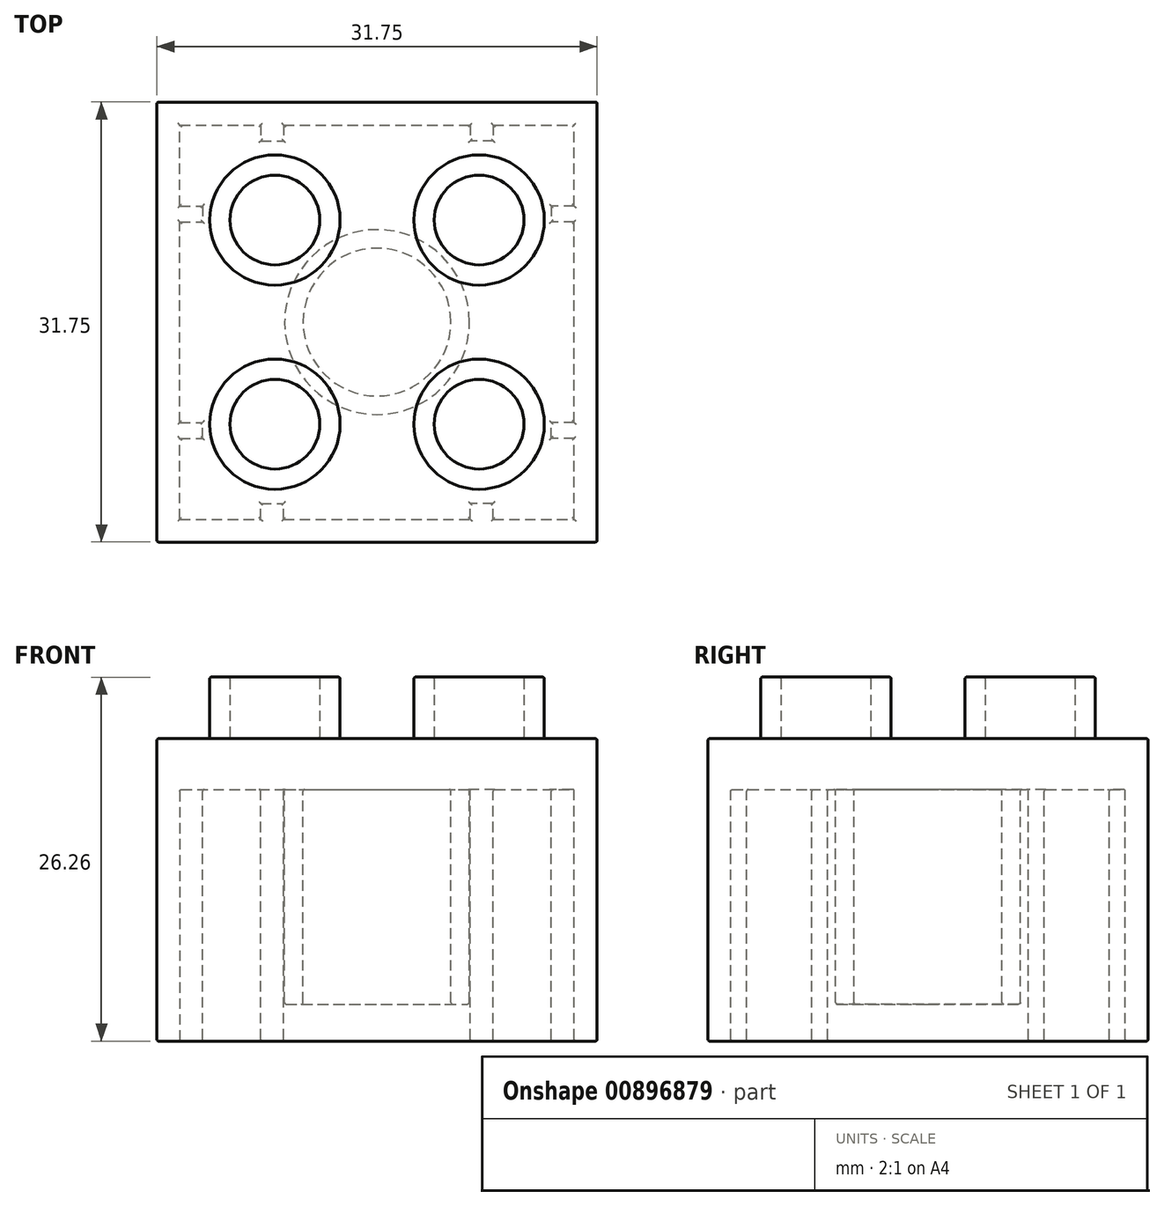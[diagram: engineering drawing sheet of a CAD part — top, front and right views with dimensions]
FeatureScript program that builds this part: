
annotation { "Feature Type Name" : "Feature", "Feature Type Description" : "" }
export const myFeature = defineFeature(function(context is Context, id is Id, definition is map)
    precondition{}
    {
        {
            var Q0;
            Q0=qCreatedBy(makeId("Top.planeOp"),FACE);
            var sketch = newSketch(context, id + "F0", { "sketchPlane" : qUnion([Q0])});
            skLineSegment(sketch, "E0.bottom", {"start": v(-34.78, 34.87) * mm, "end": v(-66.53, 34.87) * mm});
            skLineSegment(sketch, "E0.top", {"start": v(-34.78, 3.12) * mm, "end": v(-66.53, 3.12) * mm});
            skLineSegment(sketch, "E0.left", {"start": v(-34.78, 34.87) * mm, "end": v(-34.78, 3.12) * mm});
            skLineSegment(sketch, "E0.right", {"start": v(-66.53, 34.87) * mm, "end": v(-66.53, 3.12) * mm});
            skSolve(sketch);
        }
        {
            var Q0;
            Q0=makeQuery(id+"F0.imprint","IMPRINT",FACE,{"disambiguationData":[TD([[makeQuery(id+"F0.imprint","IMPRINT",EDGE,{"derivedFrom":sQuery(id+"F0.wireOp",EDGE,"E0.bottom")}),1.0]])]});
            extrude(context, id + "F1", {"entities" : qUnion([Q0]), "depth" : 21.82 * mm, "offsetDistance" : 25.4 * mm});
        }
        {
            var Q0;
            Q0=makeQuery(id+"F1.opExtrude","CAP_FACE",FACE,{"disambiguationData":[OSD([sQuery(id+"F0.wireOp",EDGE,"E0.bottom"),sQuery(id+"F0.wireOp",EDGE,"E0.top"),sQuery(id+"F0.wireOp",EDGE,"E0.left"),sQuery(id+"F0.wireOp",EDGE,"E0.right")])],"isStart":false});
            var sketch = newSketch(context, id + "F2", { "sketchPlane" : qUnion([Q0])});
            skCircle(sketch, "E1", {"center": v(-58.02, 26.36) * mm, "radius": 4.7 * mm});
            skCircle(sketch, "E2", {"center": v(-58.02, 26.36) * mm, "radius": 3.24 * mm});
            skCircle(sketch, "E3", {"center": v(-43.29, 26.36) * mm, "radius": 4.7 * mm});
            skCircle(sketch, "E4", {"center": v(-43.29, 26.36) * mm, "radius": 3.24 * mm});
            skCircle(sketch, "E5", {"center": v(-58.02, 11.63) * mm, "radius": 4.7 * mm});
            skCircle(sketch, "E6", {"center": v(-58.02, 11.63) * mm, "radius": 3.24 * mm});
            skCircle(sketch, "E7", {"center": v(-43.29, 11.63) * mm, "radius": 4.7 * mm});
            skCircle(sketch, "E8", {"center": v(-43.29, 11.63) * mm, "radius": 3.24 * mm});
            skSolve(sketch);
        }
        {
            var Q0;
            Q0=makeQuery(id+"F2.imprint","IMPRINT",FACE,{"disambiguationData":[TD([[makeQuery(id+"F2.imprint","IMPRINT",EDGE,{"derivedFrom":sQuery(id+"F2.wireOp",EDGE,"E7")}),1.0]])]});
            var Q1;
            Q1=makeQuery(id+"F2.imprint","IMPRINT",FACE,{"disambiguationData":[TD([[makeQuery(id+"F2.imprint","IMPRINT",EDGE,{"derivedFrom":sQuery(id+"F2.wireOp",EDGE,"E5")}),1.0]])]});
            var Q2;
            Q2=makeQuery(id+"F2.imprint","IMPRINT",FACE,{"disambiguationData":[TD([[makeQuery(id+"F2.imprint","IMPRINT",EDGE,{"derivedFrom":sQuery(id+"F2.wireOp",EDGE,"E1")}),1.0]])]});
            var Q3;
            Q3=makeQuery(id+"F2.imprint","IMPRINT",FACE,{"disambiguationData":[TD([[makeQuery(id+"F2.imprint","IMPRINT",EDGE,{"derivedFrom":sQuery(id+"F2.wireOp",EDGE,"E3")}),1.0]])]});
            extrude(context, id + "F3", {"entities" : qUnion([Q0, Q1, Q2, Q3]), "operationType" : NewBodyOperationType.ADD, "depth" : 4.44 * mm, "offsetDistance" : 25.4 * mm});
        }
        {
            var Q0;
            Q0=makeQuery(id+"F1.opExtrude","CAP_FACE",FACE,{"disambiguationData":[OSD([sQuery(id+"F0.wireOp",EDGE,"E0.bottom"),sQuery(id+"F0.wireOp",EDGE,"E0.top"),sQuery(id+"F0.wireOp",EDGE,"E0.left"),sQuery(id+"F0.wireOp",EDGE,"E0.right")])],"isStart":true});
            var sketch = newSketch(context, id + "F4", { "sketchPlane" : qUnion([Q0])});
            skLineSegment(sketch, "E9.bottom", {"start": v(-64.88, -4.77) * mm, "end": v(-36.43, -4.77) * mm});
            skLineSegment(sketch, "E9.top", {"start": v(-64.88, -33.22) * mm, "end": v(-36.43, -33.22) * mm});
            skLineSegment(sketch, "E9.left", {"start": v(-64.88, -4.77) * mm, "end": v(-64.88, -33.22) * mm});
            skLineSegment(sketch, "E9.right", {"start": v(-36.43, -4.77) * mm, "end": v(-36.43, -33.22) * mm});
            skSolve(sketch);
        }
        {
            var Q0;
            Q0=makeQuery(id+"F4.imprint","IMPRINT",FACE,{"disambiguationData":[TD([[makeQuery(id+"F4.imprint","IMPRINT",EDGE,{"derivedFrom":sQuery(id+"F4.wireOp",EDGE,"E9.bottom")}),-1.0]])]});
            extrude(context, id + "F5", {"entities" : qUnion([Q0]), "operationType" : NewBodyOperationType.REMOVE, "oppositeDirection" : true, "depth" : 18.16 * mm, "offsetDistance" : 25.4 * mm});
        }
        {
            var Q0;
            Q0=makeQuery(id+"F5.boolean.opBoolean","COPY",FACE,{"derivedFrom":makeQuery(id+"F5.opExtrude","CAP_FACE",FACE,{"disambiguationData":[OSD([sQuery(id+"F4.wireOp",EDGE,"E9.bottom"),sQuery(id+"F4.wireOp",EDGE,"E9.top"),sQuery(id+"F4.wireOp",EDGE,"E9.left"),sQuery(id+"F4.wireOp",EDGE,"E9.right")])],"isStart":false})});
            var sketch = newSketch(context, id + "F6", { "sketchPlane" : qUnion([Q0])});
            skCircle(sketch, "E10", {"center": v(-50.65, -19) * mm, "radius": 5.33 * mm});
            skCircle(sketch, "E11", {"center": v(-50.65, -19) * mm, "radius": 6.67 * mm});
            skSolve(sketch);
        }
        {
            var Q0;
            Q0=makeQuery(id+"F6.imprint","IMPRINT",FACE,{"disambiguationData":[TD([[makeQuery(id+"F6.imprint","IMPRINT",EDGE,{"derivedFrom":sQuery(id+"F6.wireOp",EDGE,"E10")}),-1.0]])]});
            extrude(context, id + "F7", {"entities" : qUnion([Q0]), "operationType" : NewBodyOperationType.ADD, "depth" : 15.5 * mm, "offsetDistance" : 25.4 * mm});
        }
        {
            var Q0;
            {var subQ0=sQuery(id+"F4.wireOp",EDGE,"E9.right");var subQ1=sQuery(id+"F4.wireOp",EDGE,"E9.left");var subQ2=sQuery(id+"F4.wireOp",EDGE,"E9.top");var subQ3=sQuery(id+"F4.wireOp",EDGE,"E9.bottom");Q0=makeQuery(id+"F7.boolean.opBoolean","SPLIT",FACE,{"disambiguationData":[TD([makeQuery(id+"F5.boolean.opBoolean","COPY",FACE,{"derivedFrom":makeQuery(id+"F5.opExtrude","SWEPT_FACE",FACE,{"disambiguationData":[OSD([subQ3])]})})])],"derivedFrom":makeQuery(id+"F5.boolean.opBoolean","COPY",FACE,{"derivedFrom":makeQuery(id+"F5.opExtrude","CAP_FACE",FACE,{"disambiguationData":[OSD([subQ3,subQ2,subQ1,subQ0])],"isStart":false})})});}
            var sketch = newSketch(context, id + "F8", { "sketchPlane" : qUnion([Q0])});
            skLineSegment(sketch, "E12.bottom", {"start": v(-36.43, -10.61) * mm, "end": v(-38.08, -10.61) * mm});
            skLineSegment(sketch, "E12.top", {"start": v(-36.43, -11.75) * mm, "end": v(-38.08, -11.75) * mm});
            skLineSegment(sketch, "E12.left", {"start": v(-36.43, -10.61) * mm, "end": v(-36.43, -11.75) * mm});
            skLineSegment(sketch, "E12.right", {"start": v(-38.08, -10.61) * mm, "end": v(-38.08, -11.75) * mm});
            skLineSegment(sketch, "E13.bottom", {"start": v(-42.27, -4.77) * mm, "end": v(-43.92, -4.77) * mm});
            skLineSegment(sketch, "E13.top", {"start": v(-42.27, -5.91) * mm, "end": v(-43.92, -5.91) * mm});
            skLineSegment(sketch, "E13.left", {"start": v(-42.27, -4.77) * mm, "end": v(-42.27, -5.91) * mm});
            skLineSegment(sketch, "E13.right", {"start": v(-43.92, -4.77) * mm, "end": v(-43.92, -5.91) * mm});
            skLineSegment(sketch, "E14", {"start": v(-50.65, -4.77) * mm, "end": v(-50.65, -33.22) * mm});
            skLineSegment(sketch, "E15", {"start": v(-64.88, -19) * mm, "end": v(-36.43, -19) * mm});
            skLineSegment(sketch, "E16.MirrorCS", {"start": v(-59.04, -4.77) * mm, "end": v(-59.04, -5.91) * mm});
            skLineSegment(sketch, "E17.MirrorCS", {"start": v(-59.04, -4.77) * mm, "end": v(-57.38, -4.77) * mm});
            skLineSegment(sketch, "E18.MirrorCS", {"start": v(-57.38, -4.77) * mm, "end": v(-57.38, -5.91) * mm});
            skLineSegment(sketch, "E19.MirrorCS", {"start": v(-59.04, -5.91) * mm, "end": v(-57.38, -5.91) * mm});
            skLineSegment(sketch, "E20.MirrorCS", {"start": v(-63.23, -10.61) * mm, "end": v(-63.23, -11.75) * mm});
            skLineSegment(sketch, "E21.MirrorCS", {"start": v(-64.88, -10.61) * mm, "end": v(-63.23, -10.61) * mm});
            skLineSegment(sketch, "E22.MirrorCS", {"start": v(-64.88, -10.61) * mm, "end": v(-64.88, -11.75) * mm});
            skLineSegment(sketch, "E23.MirrorCS", {"start": v(-64.88, -11.75) * mm, "end": v(-63.23, -11.75) * mm});
            skLineSegment(sketch, "E24.MirrorCS", {"start": v(-42.27, -33.22) * mm, "end": v(-42.27, -32.07) * mm});
            skLineSegment(sketch, "E25.MirrorCS", {"start": v(-43.92, -33.22) * mm, "end": v(-43.92, -32.07) * mm});
            skLineSegment(sketch, "E26.MirrorCS", {"start": v(-42.27, -33.22) * mm, "end": v(-43.92, -33.22) * mm});
            skLineSegment(sketch, "E27.MirrorCS", {"start": v(-42.27, -32.07) * mm, "end": v(-43.92, -32.07) * mm});
            skLineSegment(sketch, "E28.MirrorCS", {"start": v(-38.08, -27.37) * mm, "end": v(-38.08, -26.23) * mm});
            skLineSegment(sketch, "E29.MirrorCS", {"start": v(-36.43, -27.37) * mm, "end": v(-38.08, -27.37) * mm});
            skLineSegment(sketch, "E30.MirrorCS", {"start": v(-36.43, -27.37) * mm, "end": v(-36.43, -26.23) * mm});
            skLineSegment(sketch, "E31.MirrorCS", {"start": v(-36.43, -26.23) * mm, "end": v(-38.08, -26.23) * mm});
            skLineSegment(sketch, "E32.MirrorCS", {"start": v(-63.23, -27.37) * mm, "end": v(-63.23, -26.23) * mm});
            skLineSegment(sketch, "E33.MirrorCS", {"start": v(-64.88, -26.23) * mm, "end": v(-63.23, -26.23) * mm});
            skLineSegment(sketch, "E34.MirrorCS", {"start": v(-64.88, -27.37) * mm, "end": v(-64.88, -26.23) * mm});
            skLineSegment(sketch, "E35.MirrorCS", {"start": v(-64.88, -27.37) * mm, "end": v(-63.23, -27.37) * mm});
            skLineSegment(sketch, "E36.MirrorCS", {"start": v(-59.04, -33.22) * mm, "end": v(-59.04, -32.07) * mm});
            skLineSegment(sketch, "E37.MirrorCS", {"start": v(-59.04, -33.22) * mm, "end": v(-57.38, -33.22) * mm});
            skLineSegment(sketch, "E38.MirrorCS", {"start": v(-57.38, -33.22) * mm, "end": v(-57.38, -32.07) * mm});
            skLineSegment(sketch, "E39.MirrorCS", {"start": v(-59.04, -32.07) * mm, "end": v(-57.38, -32.07) * mm});
            skSolve(sketch);
        }
        {
            var Q0;
            Q0=makeQuery(id+"F8.imprint","IMPRINT",FACE,{"disambiguationData":[TD([[makeQuery(id+"F8.imprint","IMPRINT",EDGE,{"derivedFrom":sQuery(id+"F8.wireOp",EDGE,"E13.bottom")}),-1.0]])]});
            var Q1;
            Q1=makeQuery(id+"F8.imprint","IMPRINT",FACE,{"disambiguationData":[TD([[makeQuery(id+"F8.imprint","IMPRINT",EDGE,{"derivedFrom":sQuery(id+"F8.wireOp",EDGE,"E12.bottom")}),1.0]])]});
            var Q2;
            Q2=makeQuery(id+"F8.imprint","IMPRINT",FACE,{"disambiguationData":[TD([[makeQuery(id+"F8.imprint","IMPRINT",EDGE,{"derivedFrom":sQuery(id+"F8.wireOp",EDGE,"E16.MirrorCS")}),1.0]])]});
            var Q3;
            Q3=makeQuery(id+"F8.imprint","IMPRINT",FACE,{"disambiguationData":[TD([[makeQuery(id+"F8.imprint","IMPRINT",EDGE,{"derivedFrom":sQuery(id+"F8.wireOp",EDGE,"E20.MirrorCS")}),-1.0]])]});
            var Q4;
            Q4=makeQuery(id+"F8.imprint","IMPRINT",FACE,{"disambiguationData":[TD([[makeQuery(id+"F8.imprint","IMPRINT",EDGE,{"derivedFrom":sQuery(id+"F8.wireOp",EDGE,"E32.MirrorCS")}),1.0]])]});
            var Q5;
            Q5=makeQuery(id+"F8.imprint","IMPRINT",FACE,{"disambiguationData":[TD([[makeQuery(id+"F8.imprint","IMPRINT",EDGE,{"derivedFrom":sQuery(id+"F8.wireOp",EDGE,"E36.MirrorCS")}),-1.0]])]});
            var Q6;
            Q6=makeQuery(id+"F8.imprint","IMPRINT",FACE,{"disambiguationData":[TD([[makeQuery(id+"F8.imprint","IMPRINT",EDGE,{"derivedFrom":sQuery(id+"F8.wireOp",EDGE,"E24.MirrorCS")}),1.0]])]});
            var Q7;
            Q7=makeQuery(id+"F8.imprint","IMPRINT",FACE,{"disambiguationData":[TD([[makeQuery(id+"F8.imprint","IMPRINT",EDGE,{"derivedFrom":sQuery(id+"F8.wireOp",EDGE,"E28.MirrorCS")}),-1.0]])]});
            extrude(context, id + "F9", {"entities" : qUnion([Q0, Q1, Q2, Q3, Q4, Q5, Q6, Q7]), "operationType" : NewBodyOperationType.ADD, "depth" : 18.16 * mm, "offsetDistance" : 25.4 * mm});
        }
        {
            var Q0;
            Q0=makeQuery(id+"F3.opExtrude","SWEPT_FACE",FACE,{"disambiguationData":[OSD([sQuery(id+"F2.wireOp",EDGE,"E1")])]});
            var Q1;
            Q1=makeQuery(id+"F3.opExtrude","SWEPT_FACE",FACE,{"disambiguationData":[OSD([sQuery(id+"F2.wireOp",EDGE,"E2")])]});
            var Q2;
            Q2=makeQuery(id+"F3.opExtrude","SWEPT_FACE",FACE,{"disambiguationData":[OSD([sQuery(id+"F2.wireOp",EDGE,"E3")])]});
            var Q3;
            Q3=makeQuery(id+"F3.opExtrude","SWEPT_FACE",FACE,{"disambiguationData":[OSD([sQuery(id+"F2.wireOp",EDGE,"E4")])]});
            var Q4;
            Q4=makeQuery(id+"F3.opExtrude","SWEPT_FACE",FACE,{"disambiguationData":[OSD([sQuery(id+"F2.wireOp",EDGE,"E7")])]});
            var Q5;
            Q5=makeQuery(id+"F3.opExtrude","SWEPT_FACE",FACE,{"disambiguationData":[OSD([sQuery(id+"F2.wireOp",EDGE,"E8")])]});
            var Q6;
            Q6=makeQuery(id+"F3.opExtrude","SWEPT_FACE",FACE,{"disambiguationData":[OSD([sQuery(id+"F2.wireOp",EDGE,"E5")])]});
            var Q7;
            Q7=makeQuery(id+"F3.opExtrude","SWEPT_FACE",FACE,{"disambiguationData":[OSD([sQuery(id+"F2.wireOp",EDGE,"E6")])]});
            var Q8;
            {var subQ0=sQuery(id+"F0.wireOp",EDGE,"E0.left");var subQ1=sQuery(id+"F0.wireOp",EDGE,"E0.top");var subQ2=sQuery(id+"F0.wireOp",EDGE,"E0.right");var subQ3=sQuery(id+"F0.wireOp",EDGE,"E0.bottom");Q8=makeQuery(id+"F3.boolean.opBoolean","SPLIT",FACE,{"disambiguationData":[TD([makeQuery(id+"F1.opExtrude","SWEPT_FACE",FACE,{"disambiguationData":[OSD([subQ3])]})])],"derivedFrom":makeQuery(id+"F1.opExtrude","CAP_FACE",FACE,{"disambiguationData":[OSD([subQ3,subQ1,subQ0,subQ2])],"isStart":false})});}
            var Q9;
            Q9=makeQuery(id+"F1.opExtrude","SWEPT_FACE",FACE,{"disambiguationData":[OSD([sQuery(id+"F0.wireOp",EDGE,"E0.right")])]});
            var Q10;
            Q10=makeQuery(id+"F1.opExtrude","SWEPT_FACE",FACE,{"disambiguationData":[OSD([sQuery(id+"F0.wireOp",EDGE,"E0.top")])]});
            var Q11;
            Q11=makeQuery(id+"F1.opExtrude","SWEPT_FACE",FACE,{"disambiguationData":[OSD([sQuery(id+"F0.wireOp",EDGE,"E0.left")])]});
            var Q12;
            Q12=makeQuery(id+"F1.opExtrude","SWEPT_FACE",FACE,{"disambiguationData":[OSD([sQuery(id+"F0.wireOp",EDGE,"E0.bottom")])]});
            var Q13;
            Q13=makeQuery(id+"F7.opExtrude","SWEPT_FACE",FACE,{"disambiguationData":[OSD([sQuery(id+"F6.wireOp",EDGE,"E10")])]});
            var Q14;
            Q14=makeQuery(id+"F7.opExtrude","SWEPT_FACE",FACE,{"disambiguationData":[OSD([sQuery(id+"F6.wireOp",EDGE,"E11")])]});
            var Q15;
            Q15=makeQuery(id+"F9.boolean.opBoolean","MERGE",FACE,{"derivedFrom":[makeQuery(id+"F1.opExtrude","CAP_FACE",FACE,{"disambiguationData":[OSD([sQuery(id+"F0.wireOp",EDGE,"E0.bottom"),sQuery(id+"F0.wireOp",EDGE,"E0.top"),sQuery(id+"F0.wireOp",EDGE,"E0.left"),sQuery(id+"F0.wireOp",EDGE,"E0.right")])],"isStart":true}),makeQuery(id+"F9.opExtrude","CAP_FACE",FACE,{"disambiguationData":[OSD([sQuery(id+"F8.wireOp",EDGE,"E12.bottom"),sQuery(id+"F8.wireOp",EDGE,"E12.top"),sQuery(id+"F8.wireOp",EDGE,"E12.left"),sQuery(id+"F8.wireOp",EDGE,"E12.right")])],"isStart":false}),makeQuery(id+"F9.opExtrude","CAP_FACE",FACE,{"disambiguationData":[OSD([sQuery(id+"F8.wireOp",EDGE,"E13.bottom"),sQuery(id+"F8.wireOp",EDGE,"E13.top"),sQuery(id+"F8.wireOp",EDGE,"E13.left"),sQuery(id+"F8.wireOp",EDGE,"E13.right")])],"isStart":false}),makeQuery(id+"F9.opExtrude","CAP_FACE",FACE,{"disambiguationData":[OSD([sQuery(id+"F8.wireOp",EDGE,"E16.MirrorCS"),sQuery(id+"F8.wireOp",EDGE,"E17.MirrorCS"),sQuery(id+"F8.wireOp",EDGE,"E18.MirrorCS"),sQuery(id+"F8.wireOp",EDGE,"E19.MirrorCS")])],"isStart":false}),makeQuery(id+"F9.opExtrude","CAP_FACE",FACE,{"disambiguationData":[OSD([sQuery(id+"F8.wireOp",EDGE,"E20.MirrorCS"),sQuery(id+"F8.wireOp",EDGE,"E21.MirrorCS"),sQuery(id+"F8.wireOp",EDGE,"E22.MirrorCS"),sQuery(id+"F8.wireOp",EDGE,"E23.MirrorCS")])],"isStart":false}),makeQuery(id+"F9.opExtrude","CAP_FACE",FACE,{"disambiguationData":[OSD([sQuery(id+"F8.wireOp",EDGE,"E24.MirrorCS"),sQuery(id+"F8.wireOp",EDGE,"E25.MirrorCS"),sQuery(id+"F8.wireOp",EDGE,"E26.MirrorCS"),sQuery(id+"F8.wireOp",EDGE,"E27.MirrorCS")])],"isStart":false}),makeQuery(id+"F9.opExtrude","CAP_FACE",FACE,{"disambiguationData":[OSD([sQuery(id+"F8.wireOp",EDGE,"E28.MirrorCS"),sQuery(id+"F8.wireOp",EDGE,"E29.MirrorCS"),sQuery(id+"F8.wireOp",EDGE,"E30.MirrorCS"),sQuery(id+"F8.wireOp",EDGE,"E31.MirrorCS")])],"isStart":false}),makeQuery(id+"F9.opExtrude","CAP_FACE",FACE,{"disambiguationData":[OSD([sQuery(id+"F8.wireOp",EDGE,"E32.MirrorCS"),sQuery(id+"F8.wireOp",EDGE,"E33.MirrorCS"),sQuery(id+"F8.wireOp",EDGE,"E34.MirrorCS"),sQuery(id+"F8.wireOp",EDGE,"E35.MirrorCS")])],"isStart":false}),makeQuery(id+"F9.opExtrude","CAP_FACE",FACE,{"disambiguationData":[OSD([sQuery(id+"F8.wireOp",EDGE,"E36.MirrorCS"),sQuery(id+"F8.wireOp",EDGE,"E37.MirrorCS"),sQuery(id+"F8.wireOp",EDGE,"E38.MirrorCS"),sQuery(id+"F8.wireOp",EDGE,"E39.MirrorCS")])],"isStart":false})]});
            fillet(context, id + "F10", {"entities" : qUnion([Q0, Q1, Q2, Q3, Q4, Q5, Q6, Q7, Q8, Q9, Q10, Q11, Q12, Q13, Q14, Q15]), "radius" : 0.13 * mm, "tangentPropagation" : true, "allowEdgeOverflow" : false});
        }
        {
            var Q0;
            {var subQ0=sQuery(id+"F4.wireOp",EDGE,"E9.right");var subQ1=sQuery(id+"F4.wireOp",EDGE,"E9.left");var subQ2=sQuery(id+"F4.wireOp",EDGE,"E9.top");var subQ3=sQuery(id+"F4.wireOp",EDGE,"E9.bottom");Q0=makeQuery(id+"F7.boolean.opBoolean","SPLIT",FACE,{"disambiguationData":[TD([makeQuery(id+"F5.boolean.opBoolean","COPY",FACE,{"derivedFrom":makeQuery(id+"F5.opExtrude","SWEPT_FACE",FACE,{"disambiguationData":[OSD([subQ3])]})})])],"derivedFrom":makeQuery(id+"F5.boolean.opBoolean","COPY",FACE,{"derivedFrom":makeQuery(id+"F5.opExtrude","CAP_FACE",FACE,{"disambiguationData":[OSD([subQ3,subQ2,subQ1,subQ0])],"isStart":false})})});}
            fillet(context, id + "F11", {"entities" : qUnion([Q0]), "radius" : 0.13 * mm, "tangentPropagation" : true, "allowEdgeOverflow" : false});
        }
    });
